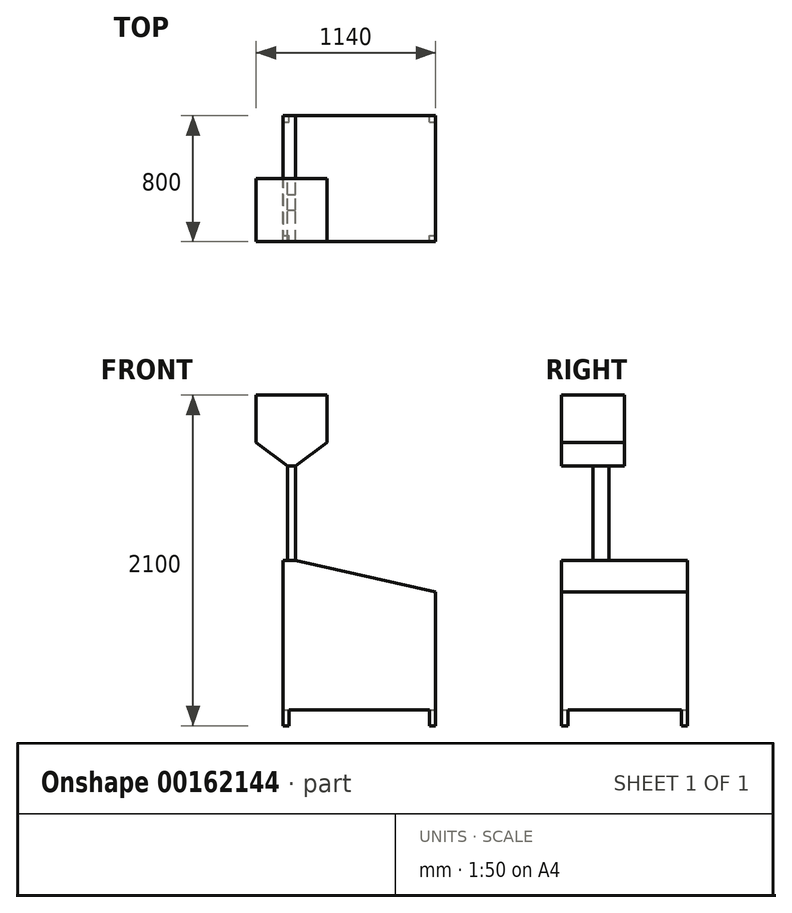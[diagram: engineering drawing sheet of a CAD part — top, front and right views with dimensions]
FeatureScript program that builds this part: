
annotation { "Feature Type Name" : "Feature", "Feature Type Description" : "" }
export const myFeature = defineFeature(function(context is Context, id is Id, definition is map)
    precondition{}
    {
        {
            var Q0;
            Q0=qCreatedBy(makeId("Front.planeOp"),FACE);
            var sketch = newSketch(context, id + "F0", { "sketchPlane" : qUnion([Q0])});
            skLineSegment(sketch, "E0", {"start": v(0, 0) * mm, "end": v(0, 1050) * mm});
            skLineSegment(sketch, "E1", {"start": v(970, 850) * mm, "end": v(970, 0) * mm});
            skLineSegment(sketch, "E2", {"start": v(970, 0) * mm, "end": v(930, 0) * mm});
            skLineSegment(sketch, "E3", {"start": v(930, 0) * mm, "end": v(930, 100) * mm});
            skLineSegment(sketch, "E4", {"start": v(930, 100) * mm, "end": v(40, 100) * mm});
            skLineSegment(sketch, "E5", {"start": v(40, 100) * mm, "end": v(40, 0) * mm});
            skLineSegment(sketch, "E6", {"start": v(40, 0) * mm, "end": v(0, 0) * mm});
            skLineSegment(sketch, "E7", {"start": v(0, 1050) * mm, "end": v(30, 1050) * mm});
            skLineSegment(sketch, "E8", {"start": v(30, 1050) * mm, "end": v(30, 1650) * mm});
            skLineSegment(sketch, "E9", {"start": v(30, 1650) * mm, "end": v(-170, 1800) * mm});
            skLineSegment(sketch, "E10", {"start": v(-170, 1800) * mm, "end": v(-170, 2100) * mm});
            skLineSegment(sketch, "E11", {"start": v(-170, 2100) * mm, "end": v(280, 2100) * mm});
            skLineSegment(sketch, "E12", {"start": v(280, 2100) * mm, "end": v(280, 1800) * mm});
            skLineSegment(sketch, "E13", {"start": v(280, 1800) * mm, "end": v(80, 1650) * mm});
            skLineSegment(sketch, "E14", {"start": v(80, 1650) * mm, "end": v(80, 1050) * mm});
            skLineSegment(sketch, "E15", {"start": v(80, 1050) * mm, "end": v(970, 850) * mm});
            skSolve(sketch);
        }
        {
            var Q0;
            Q0 = qSketchRegion(id + "F0", true);
            extrude(context, id + "F1", {"entities" : qUnion([Q0]), "depth" : 800 * mm});
        }
        {
            var Q0;
            Q0=makeQuery(id+"F1.opExtrude","SWEPT_FACE",FACE,{"disambiguationData":[OSD([sQuery(id+"F0.wireOp",EDGE,"E1")])]});
            var sketch = newSketch(context, id + "F2", { "sketchPlane" : qUnion([Q0])});
            skLineSegment(sketch, "E16.bottom", {"start": v(-760, 0) * mm, "end": v(-40, 0) * mm});
            skLineSegment(sketch, "E16.top", {"start": v(-760, 100) * mm, "end": v(-40, 100) * mm});
            skLineSegment(sketch, "E16.left", {"start": v(-760, 0) * mm, "end": v(-760, 100) * mm});
            skLineSegment(sketch, "E16.right", {"start": v(-40, 0) * mm, "end": v(-40, 100) * mm});
            skLineSegment(sketch, "E17", {"start": v(-800, 1050) * mm, "end": v(-600, 1050) * mm});
            skLineSegment(sketch, "E18", {"start": v(-600, 1050) * mm, "end": v(-600, 1650) * mm});
            skLineSegment(sketch, "E19", {"start": v(-600, 1650) * mm, "end": v(-800, 1650) * mm});
            skLineSegment(sketch, "E20", {"start": v(-800, 1650) * mm, "end": v(-800, 2165.25) * mm});
            skLineSegment(sketch, "E21", {"start": v(-800, 2165.25) * mm, "end": v(-400.05, 2171.84) * mm});
            skLineSegment(sketch, "E22", {"start": v(-400.05, 2171.84) * mm, "end": v(-400.05, 1650) * mm});
            skLineSegment(sketch, "E23", {"start": v(-400.05, 1650) * mm, "end": v(-500, 1650) * mm});
            skLineSegment(sketch, "E24", {"start": v(-500, 1650) * mm, "end": v(-500, 1050) * mm});
            skLineSegment(sketch, "E25", {"start": v(-500, 1050) * mm, "end": v(130.56, 1050) * mm});
            skLineSegment(sketch, "E26", {"start": v(130.56, 1050) * mm, "end": v(1207.75, 1992.83) * mm});
            skLineSegment(sketch, "E27", {"start": v(1207.75, 1992.83) * mm, "end": v(48.13, 2661.81) * mm});
            skLineSegment(sketch, "E28", {"start": v(48.13, 2661.81) * mm, "end": v(-1305, 2532.38) * mm});
            skLineSegment(sketch, "E29", {"start": v(-1305, 2532.38) * mm, "end": v(-1182.62, 1232.52) * mm});
            skLineSegment(sketch, "E30", {"start": v(-1182.62, 1232.52) * mm, "end": v(-800, 1050) * mm});
            skSolve(sketch);
        }
        {
            var Q0;
            Q0 = qSketchRegion(id + "F2", true);
            extrude(context, id + "F3", {"entities" : qUnion([Q0]), "operationType" : NewBodyOperationType.REMOVE, "endBound" : BoundingType.THROUGH_ALL, "oppositeDirection" : true, "depth" : 25 * mm});
        }
    });
